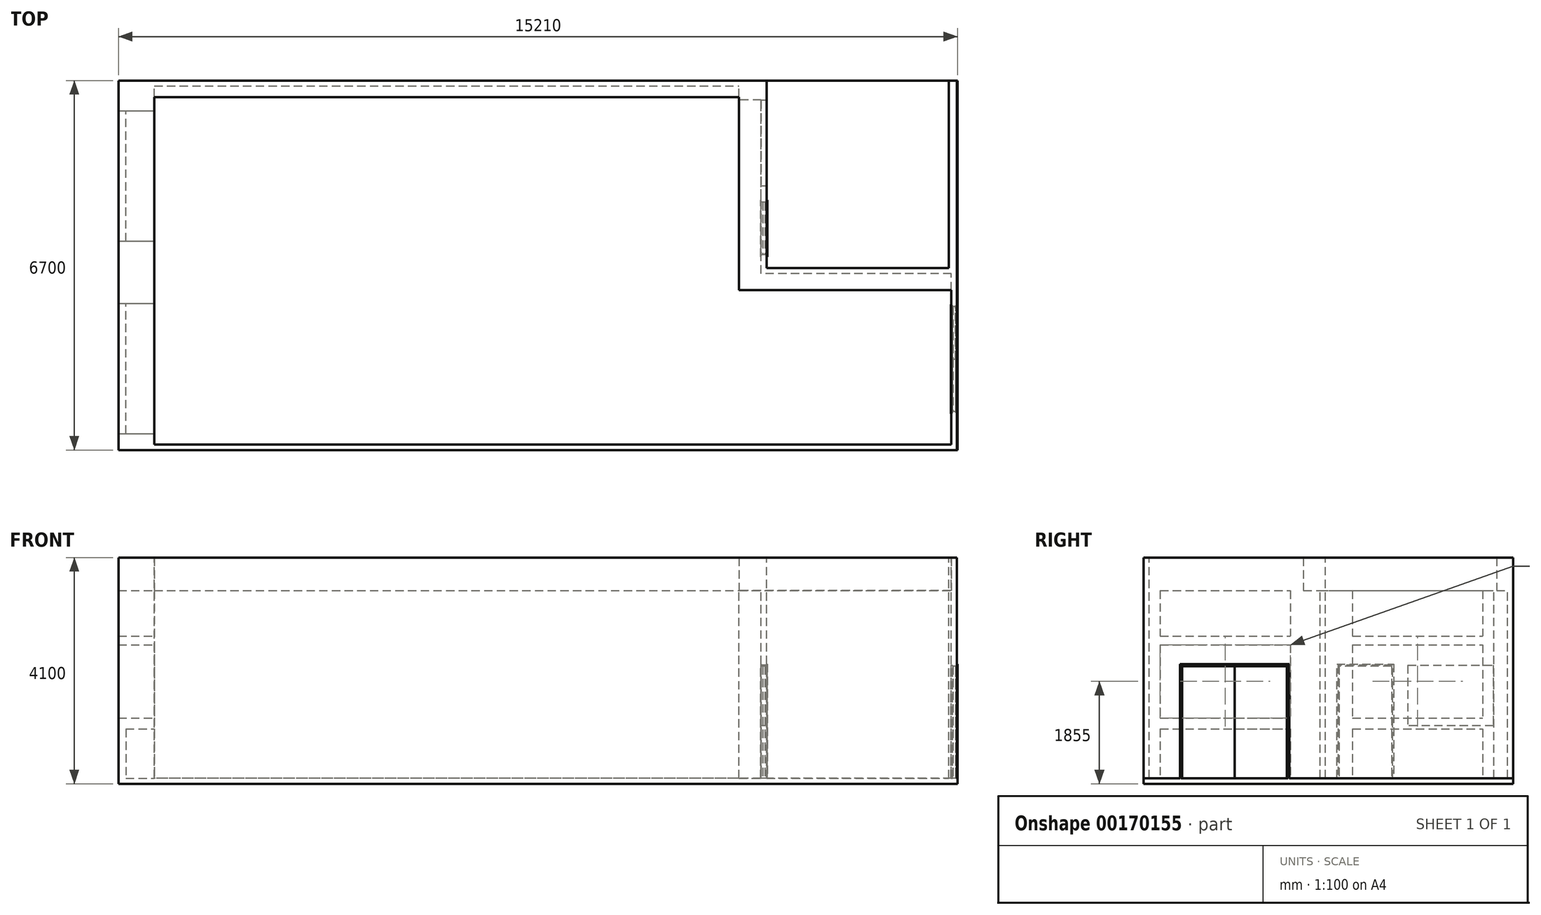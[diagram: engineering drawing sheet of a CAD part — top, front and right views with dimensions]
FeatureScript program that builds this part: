
annotation { "Feature Type Name" : "Feature", "Feature Type Description" : "" }
export const myFeature = defineFeature(function(context is Context, id is Id, definition is map)
    precondition{}
    {
        {
            var Q0;
            Q0=qCreatedBy(makeId("Right.planeOp"),FACE);
            var sketch = newSketch(context, id + "F0", { "sketchPlane" : qUnion([Q0])});
            skLineSegment(sketch, "E0", {"start": v(0, 0) * mm, "end": v(0, 4000) * mm});
            skLineSegment(sketch, "E1", {"start": v(6500, 4000) * mm, "end": v(6500, 0) * mm});
            skLineSegment(sketch, "E2", {"start": v(0, 0) * mm, "end": v(6500, 0) * mm});
            skLineSegment(sketch, "E3", {"start": v(0, 4000) * mm, "end": v(-100, 4000) * mm});
            skLineSegment(sketch, "E4", {"start": v(-100, 4000) * mm, "end": v(-100, -100) * mm});
            skLineSegment(sketch, "E5", {"start": v(-100, -100) * mm, "end": v(6600, -100) * mm});
            skLineSegment(sketch, "E6", {"start": v(6600, -100) * mm, "end": v(6600, 4000) * mm});
            skLineSegment(sketch, "E7", {"start": v(6600, 4000) * mm, "end": v(6500, 4000) * mm});
            skSolve(sketch);
        }
        {
            var Q0;
            Q0=makeQuery(id+"F0.imprint","IMPRINT",FACE,{"disambiguationData":[TD([[makeQuery(id+"F0.imprint","IMPRINT",EDGE,{"derivedFrom":sQuery(id+"F0.wireOp",EDGE,"E0")}),1.0]])]});
            extrude(context, id + "F1", {"entities" : qUnion([Q0]), "depth" : 14500 * mm});
        }
        {
            var Q0;
            Q0=makeQuery(id+"F1.opExtrude","CAP_FACE",FACE,{"disambiguationData":[OSD([sQuery(id+"F0.wireOp",EDGE,"E0"),sQuery(id+"F0.wireOp",EDGE,"E1"),sQuery(id+"F0.wireOp",EDGE,"E2"),sQuery(id+"F0.wireOp",EDGE,"E3"),sQuery(id+"F0.wireOp",EDGE,"E4"),sQuery(id+"F0.wireOp",EDGE,"E5"),sQuery(id+"F0.wireOp",EDGE,"E6"),sQuery(id+"F0.wireOp",EDGE,"E7")])],"isStart":true});
            var sketch = newSketch(context, id + "F2", { "sketchPlane" : qUnion([Q0])});
            skLineSegment(sketch, "E8.bottom", {"start": v(-6600, -100) * mm, "end": v(100, -100) * mm});
            skLineSegment(sketch, "E8.top", {"start": v(-6600, 4000) * mm, "end": v(100, 4000) * mm});
            skLineSegment(sketch, "E8.left", {"start": v(-6600, -100) * mm, "end": v(-6600, 4000) * mm});
            skLineSegment(sketch, "E8.right", {"start": v(100, -100) * mm, "end": v(100, 4000) * mm});
            skSolve(sketch);
        }
        {
            var Q0;
            Q0 = qSketchRegion(id + "F2", true);
            extrude(context, id + "F3", {"entities" : qUnion([Q0]), "operationType" : NewBodyOperationType.ADD, "depth" : 100 * mm});
        }
        {
            var Q0;
            Q0=makeQuery(id+"F1.opExtrude","CAP_FACE",FACE,{"disambiguationData":[OSD([sQuery(id+"F0.wireOp",EDGE,"E0"),sQuery(id+"F0.wireOp",EDGE,"E1"),sQuery(id+"F0.wireOp",EDGE,"E2"),sQuery(id+"F0.wireOp",EDGE,"E3"),sQuery(id+"F0.wireOp",EDGE,"E4"),sQuery(id+"F0.wireOp",EDGE,"E5"),sQuery(id+"F0.wireOp",EDGE,"E6"),sQuery(id+"F0.wireOp",EDGE,"E7")])],"isStart":false});
            var sketch = newSketch(context, id + "F4", { "sketchPlane" : qUnion([Q0])});
            skLineSegment(sketch, "E9.bottom", {"start": v(6600, -100) * mm, "end": v(3100, -100) * mm});
            skLineSegment(sketch, "E9.top", {"start": v(6600, 4000) * mm, "end": v(3100, 4000) * mm});
            skLineSegment(sketch, "E9.left", {"start": v(6600, -100) * mm, "end": v(6600, 4000) * mm});
            skLineSegment(sketch, "E9.right", {"start": v(3100, -100) * mm, "end": v(3100, 4000) * mm});
            skSolve(sketch);
        }
        {
            var Q0;
            Q0 = qSketchRegion(id + "F4", true);
            extrude(context, id + "F5", {"entities" : qUnion([Q0]), "operationType" : NewBodyOperationType.ADD, "oppositeDirection" : true, "depth" : 3500 * mm});
        }
        {
            var Q0;
            Q0=makeQuery(id+"F5.boolean.opBoolean","MERGE",FACE,{"derivedFrom":[makeQuery(id+"F3.boolean.opBoolean","MERGE",FACE,{"derivedFrom":[makeQuery(id+"F1.opExtrude","SWEPT_FACE",FACE,{"disambiguationData":[OSD([sQuery(id+"F0.wireOp",EDGE,"E3")])]}),makeQuery(id+"F1.opExtrude","SWEPT_FACE",FACE,{"disambiguationData":[OSD([sQuery(id+"F0.wireOp",EDGE,"E7")])]}),makeQuery(id+"F3.opExtrude","SWEPT_FACE",FACE,{"disambiguationData":[OSD([sQuery(id+"F2.wireOp",EDGE,"E8.top")])]})]}),makeQuery(id+"F5.opExtrude","SWEPT_FACE",FACE,{"disambiguationData":[OSD([sQuery(id+"F4.wireOp",EDGE,"E9.top")])]})]});
            var sketch = newSketch(context, id + "F6", { "sketchPlane" : qUnion([Q0])});
            skLineSegment(sketch, "E10.bottom", {"start": v(11100, 6500) * mm, "end": v(14400, 6500) * mm});
            skLineSegment(sketch, "E10.top", {"start": v(11100, 3200) * mm, "end": v(14400, 3200) * mm});
            skLineSegment(sketch, "E10.left", {"start": v(11100, 6500) * mm, "end": v(11100, 3200) * mm});
            skLineSegment(sketch, "E10.right", {"start": v(14400, 6500) * mm, "end": v(14400, 3200) * mm});
            skSolve(sketch);
        }
        {
            var Q0;
            Q0 = qSketchRegion(id + "F6", true);
            extrude(context, id + "F7", {"entities" : qUnion([Q0]), "operationType" : NewBodyOperationType.REMOVE, "oppositeDirection" : true, "depth" : 4000 * mm});
        }
        {
            var Q0;
            Q0=makeQuery(id+"F7.boolean.opBoolean","COPY",FACE,{"derivedFrom":makeQuery(id+"F7.opExtrude","SWEPT_FACE",FACE,{"disambiguationData":[OSD([sQuery(id+"F6.wireOp",EDGE,"E10.bottom")])]})});
            var sketch = newSketch(context, id + "F8", { "sketchPlane" : qUnion([Q0])});
            skLineSegment(sketch, "E11.bottom", {"start": v(11100, 4000) * mm, "end": v(14500, 4000) * mm});
            skLineSegment(sketch, "E11.top", {"start": v(11100, 0) * mm, "end": v(14500, 0) * mm});
            skLineSegment(sketch, "E11.left", {"start": v(11100, 4000) * mm, "end": v(11100, 0) * mm});
            skLineSegment(sketch, "E11.right", {"start": v(14500, 4000) * mm, "end": v(14500, 0) * mm});
            skLineSegment(sketch, "E12", {"start": v(14400, 4000) * mm, "end": v(14400, 0) * mm});
            skSolve(sketch);
        }
        {
            var Q0;
            {var subQ0=sQuery(id+"F8.wireOp",EDGE,"E11.left");Q0=makeQuery(id+"F8.imprint","IMPRINT",FACE,{"disambiguationData":[TD([[makeQuery(id+"F8.imprint","IMPRINT",EDGE,{"derivedFrom":subQ0}),-1.0]])]});}
            extrude(context, id + "F9", {"entities" : qUnion([Q0]), "operationType" : NewBodyOperationType.REMOVE, "oppositeDirection" : true, "depth" : 300 * mm});
        }
        {
            var Q0;
            Q0=makeQuery(id+"F5.boolean.opBoolean","MERGE",FACE,{"derivedFrom":[makeQuery(id+"F1.opExtrude","CAP_FACE",FACE,{"disambiguationData":[OSD([sQuery(id+"F0.wireOp",EDGE,"E0"),sQuery(id+"F0.wireOp",EDGE,"E1"),sQuery(id+"F0.wireOp",EDGE,"E2"),sQuery(id+"F0.wireOp",EDGE,"E3"),sQuery(id+"F0.wireOp",EDGE,"E4"),sQuery(id+"F0.wireOp",EDGE,"E5"),sQuery(id+"F0.wireOp",EDGE,"E6"),sQuery(id+"F0.wireOp",EDGE,"E7")])],"isStart":false}),makeQuery(id+"F5.opExtrude","CAP_FACE",FACE,{"disambiguationData":[OSD([sQuery(id+"F4.wireOp",EDGE,"E9.bottom"),sQuery(id+"F4.wireOp",EDGE,"E9.top"),sQuery(id+"F4.wireOp",EDGE,"E9.left"),sQuery(id+"F4.wireOp",EDGE,"E9.right")])],"isStart":true})]});
            var sketch = newSketch(context, id + "F10", { "sketchPlane" : qUnion([Q0])});
            skLineSegment(sketch, "E13.bottom", {"start": v(1550, 0) * mm, "end": v(2500, 0) * mm});
            skLineSegment(sketch, "E13.top", {"start": v(1550, 2020) * mm, "end": v(2500, 2020) * mm});
            skLineSegment(sketch, "E13.left", {"start": v(1550, 0) * mm, "end": v(1550, 2020) * mm});
            skLineSegment(sketch, "E13.right", {"start": v(2500, 0) * mm, "end": v(2500, 2020) * mm});
            skLineSegment(sketch, "E14", {"start": v(2500, 0) * mm, "end": v(2540, 0) * mm});
            skLineSegment(sketch, "E15", {"start": v(2540, 0) * mm, "end": v(2540, 2020) * mm});
            skLineSegment(sketch, "E16", {"start": v(2540, 2020) * mm, "end": v(2540, 2070) * mm});
            skLineSegment(sketch, "E17", {"start": v(2540, 2070) * mm, "end": v(1550, 2070) * mm});
            skLineSegment(sketch, "E18", {"start": v(1550, -782.26) * mm, "end": v(1550, 1451.07) * mm, "construction": true});
            skLineSegment(sketch, "E19.MirrorCS", {"start": v(600, 0) * mm, "end": v(600, 2020) * mm});
            skLineSegment(sketch, "E20.MirrorCS", {"start": v(560, 0) * mm, "end": v(560, 2020) * mm});
            skLineSegment(sketch, "E21.MirrorCS", {"start": v(600, 0) * mm, "end": v(560, 0) * mm});
            skLineSegment(sketch, "E22.MirrorCS", {"start": v(560, 2070) * mm, "end": v(1550, 2070) * mm});
            skLineSegment(sketch, "E23.MirrorCS", {"start": v(1550, 2020) * mm, "end": v(600, 2020) * mm});
            skLineSegment(sketch, "E24.MirrorCS", {"start": v(560, 2020) * mm, "end": v(560, 2070) * mm});
            skLineSegment(sketch, "E25", {"start": v(600, 2020) * mm, "end": v(596, 2020) * mm});
            skLineSegment(sketch, "E26", {"start": v(596, 2020) * mm, "end": v(596, 0) * mm});
            skLineSegment(sketch, "E27", {"start": v(2500, 2020) * mm, "end": v(2504, 2020) * mm});
            skLineSegment(sketch, "E28", {"start": v(2504, 2020) * mm, "end": v(2504, 0) * mm});
            skLineSegment(sketch, "E29", {"start": v(2520, 0) * mm, "end": v(2520, 2050) * mm});
            skPoint(sketch, "E29.endSnap0", {"position": v(2520, 0) * mm});
            skLineSegment(sketch, "E30", {"start": v(2520, 2050) * mm, "end": v(580, 2050) * mm});
            skLineSegment(sketch, "E31", {"start": v(580, 2050) * mm, "end": v(580, 0) * mm});
            skSolve(sketch);
        }
        {
            var Q0;
            {var subQ5=sQuery(id+"F10.wireOp",EDGE,"E15");Q0=makeQuery(id+"F10.imprint","IMPRINT",FACE,{"disambiguationData":[TD([[makeQuery(id+"F10.imprint","IMPRINT",EDGE,{"derivedFrom":subQ5}),1.0]])]});}
            extrude(context, id + "F11", {"entities" : qUnion([Q0]), "oppositeDirection" : true, "depth" : 60 * mm, "hasSecondDirection" : true, "secondDirectionOppositeDirection" : false, "secondDirectionDepth" : 60 * mm});
        }
        {
            var Q0;
            Q0=makeQuery(id+"F5.boolean.opBoolean","MERGE",FACE,{"derivedFrom":[makeQuery(id+"F1.opExtrude","CAP_FACE",FACE,{"disambiguationData":[OSD([sQuery(id+"F0.wireOp",EDGE,"E0"),sQuery(id+"F0.wireOp",EDGE,"E1"),sQuery(id+"F0.wireOp",EDGE,"E2"),sQuery(id+"F0.wireOp",EDGE,"E3"),sQuery(id+"F0.wireOp",EDGE,"E4"),sQuery(id+"F0.wireOp",EDGE,"E5"),sQuery(id+"F0.wireOp",EDGE,"E6"),sQuery(id+"F0.wireOp",EDGE,"E7")])],"isStart":false}),makeQuery(id+"F5.opExtrude","CAP_FACE",FACE,{"disambiguationData":[OSD([sQuery(id+"F4.wireOp",EDGE,"E9.bottom"),sQuery(id+"F4.wireOp",EDGE,"E9.top"),sQuery(id+"F4.wireOp",EDGE,"E9.left"),sQuery(id+"F4.wireOp",EDGE,"E9.right")])],"isStart":true})]});
            var sketch = newSketch(context, id + "F12", { "sketchPlane" : qUnion([Q0])});
            skLineSegment(sketch, "E32", {"start": v(2520, 0) * mm, "end": v(2520, 2050) * mm});
            skLineSegment(sketch, "E33", {"start": v(580, 0) * mm, "end": v(580, 2050) * mm});
            skLineSegment(sketch, "E34", {"start": v(580, 2050) * mm, "end": v(2520, 2050) * mm});
            skLineSegment(sketch, "E35", {"start": v(600, 2030) * mm, "end": v(2500, 2030) * mm});
            skLineSegment(sketch, "E36", {"start": v(2500, 2030) * mm, "end": v(2500, 0) * mm});
            skLineSegment(sketch, "E37", {"start": v(2500, 0) * mm, "end": v(2520, 0) * mm});
            skLineSegment(sketch, "E38", {"start": v(600, 2030) * mm, "end": v(600, 0) * mm});
            skLineSegment(sketch, "E39", {"start": v(600, 0) * mm, "end": v(580, 0) * mm});
            skSolve(sketch);
        }
        {
            var Q0;
            Q0=makeQuery(id+"F12.imprint","IMPRINT",FACE,{"disambiguationData":[TD([[makeQuery(id+"F12.imprint","IMPRINT",EDGE,{"derivedFrom":sQuery(id+"F12.wireOp",EDGE,"E32")}),1.0]])]});
            extrude(context, id + "F13", {"entities" : qUnion([Q0]), "operationType" : NewBodyOperationType.ADD, "depth" : 30 * mm, "hasSecondDirection" : true, "secondDirectionOppositeDirection" : true, "secondDirectionDepth" : 30 * mm});
        }
        {
            var Q0;
            Q0=makeQuery(id+"F5.boolean.opBoolean","MERGE",FACE,{"derivedFrom":[makeQuery(id+"F1.opExtrude","CAP_FACE",FACE,{"disambiguationData":[OSD([sQuery(id+"F0.wireOp",EDGE,"E0"),sQuery(id+"F0.wireOp",EDGE,"E1"),sQuery(id+"F0.wireOp",EDGE,"E2"),sQuery(id+"F0.wireOp",EDGE,"E3"),sQuery(id+"F0.wireOp",EDGE,"E4"),sQuery(id+"F0.wireOp",EDGE,"E5"),sQuery(id+"F0.wireOp",EDGE,"E6"),sQuery(id+"F0.wireOp",EDGE,"E7")])],"isStart":false}),makeQuery(id+"F5.opExtrude","CAP_FACE",FACE,{"disambiguationData":[OSD([sQuery(id+"F4.wireOp",EDGE,"E9.bottom"),sQuery(id+"F4.wireOp",EDGE,"E9.top"),sQuery(id+"F4.wireOp",EDGE,"E9.left"),sQuery(id+"F4.wireOp",EDGE,"E9.right")])],"isStart":true})]});
            var sketch = newSketch(context, id + "F14", { "sketchPlane" : qUnion([Q0])});
            skLineSegment(sketch, "E40", {"start": v(-100, 4000) * mm, "end": v(0, 4000) * mm});
            skLineSegment(sketch, "E41", {"start": v(0, 4000) * mm, "end": v(0, 0) * mm});
            skLineSegment(sketch, "E42", {"start": v(0, 0) * mm, "end": v(3100, 0) * mm});
            skLineSegment(sketch, "E43", {"start": v(3100, 0) * mm, "end": v(3100, 4000) * mm});
            skLineSegment(sketch, "E44", {"start": v(3100, 4000) * mm, "end": v(3300, 4000) * mm});
            skLineSegment(sketch, "E45", {"start": v(3300, 4000) * mm, "end": v(3300, 0) * mm});
            skLineSegment(sketch, "E46", {"start": v(3300, 0) * mm, "end": v(3300, -100) * mm});
            skLineSegment(sketch, "E47", {"start": v(3300, -100) * mm, "end": v(-100, -100) * mm});
            skLineSegment(sketch, "E48", {"start": v(-100, -100) * mm, "end": v(-100, 4000) * mm});
            skSolve(sketch);
        }
        {
            var Q0;
            Q0=makeQuery(id+"F14.imprint","IMPRINT",FACE,{"disambiguationData":[TD([[makeQuery(id+"F14.imprint","IMPRINT",EDGE,{"derivedFrom":sQuery(id+"F14.wireOp",EDGE,"E40")}),1.0]])]});
            var sketch = newSketch(context, id + "F15", { "sketchPlane" : qUnion([Q0])});
            skLineSegment(sketch, "E49", {"start": v(0, 0) * mm, "end": v(0, 4000) * mm});
            skLineSegment(sketch, "E50", {"start": v(0, 4000) * mm, "end": v(3100, 4000) * mm});
            skLineSegment(sketch, "E51", {"start": v(3100, 4000) * mm, "end": v(3100, 0) * mm});
            skLineSegment(sketch, "E52", {"start": v(3100, 0) * mm, "end": v(2540, 0) * mm});
            skLineSegment(sketch, "E53", {"start": v(2540, 0) * mm, "end": v(2540, 2070) * mm});
            skLineSegment(sketch, "E54", {"start": v(2540, 2070) * mm, "end": v(560, 2070) * mm});
            skLineSegment(sketch, "E55", {"start": v(560, 2070) * mm, "end": v(560, 0) * mm});
            skLineSegment(sketch, "E56", {"start": v(560, 0) * mm, "end": v(0, 0) * mm});
            skSolve(sketch);
        }
        {
            var Q0;
            Q0=makeQuery(id+"F15.imprint","IMPRINT",FACE,{"disambiguationData":[TD([[makeQuery(id+"F15.imprint","IMPRINT",EDGE,{"derivedFrom":sQuery(id+"F15.wireOp",EDGE,"E49")}),-1.0]])]});
            extrude(context, id + "F16", {"entities" : qUnion([Q0]), "operationType" : NewBodyOperationType.ADD, "oppositeDirection" : true, "depth" : 50 * mm});
        }
        {
            var Q0;
            Q0=makeQuery(id+"F16.boolean.opBoolean","MERGE",FACE,{"derivedFrom":[makeQuery(id+"F5.boolean.opBoolean","MERGE",FACE,{"derivedFrom":[makeQuery(id+"F1.opExtrude","CAP_FACE",FACE,{"disambiguationData":[OSD([sQuery(id+"F0.wireOp",EDGE,"E0"),sQuery(id+"F0.wireOp",EDGE,"E1"),sQuery(id+"F0.wireOp",EDGE,"E2"),sQuery(id+"F0.wireOp",EDGE,"E3"),sQuery(id+"F0.wireOp",EDGE,"E4"),sQuery(id+"F0.wireOp",EDGE,"E5"),sQuery(id+"F0.wireOp",EDGE,"E6"),sQuery(id+"F0.wireOp",EDGE,"E7")])],"isStart":false}),makeQuery(id+"F5.opExtrude","CAP_FACE",FACE,{"disambiguationData":[OSD([sQuery(id+"F4.wireOp",EDGE,"E9.bottom"),sQuery(id+"F4.wireOp",EDGE,"E9.top"),sQuery(id+"F4.wireOp",EDGE,"E9.left"),sQuery(id+"F4.wireOp",EDGE,"E9.right")])],"isStart":true})]}),makeQuery(id+"F16.opExtrude","CAP_FACE",FACE,{"disambiguationData":[OSD([sQuery(id+"F15.wireOp",EDGE,"E49"),sQuery(id+"F15.wireOp",EDGE,"E50"),sQuery(id+"F15.wireOp",EDGE,"E51"),sQuery(id+"F15.wireOp",EDGE,"E52"),sQuery(id+"F15.wireOp",EDGE,"E53"),sQuery(id+"F15.wireOp",EDGE,"E54"),sQuery(id+"F15.wireOp",EDGE,"E55"),sQuery(id+"F15.wireOp",EDGE,"E56")])],"isStart":true})]});
            var sketch = newSketch(context, id + "F17", { "sketchPlane" : qUnion([Q0])});
            skLineSegment(sketch, "E57.bottom", {"start": v(-100, 4000) * mm, "end": v(6600, 4000) * mm});
            skLineSegment(sketch, "E57.top", {"start": v(-100, -100) * mm, "end": v(6600, -100) * mm});
            skLineSegment(sketch, "E57.left", {"start": v(-100, 4000) * mm, "end": v(-100, -100) * mm});
            skLineSegment(sketch, "E57.right", {"start": v(6600, 4000) * mm, "end": v(6600, -100) * mm});
            skLineSegment(sketch, "E58.bottom", {"start": v(560, 2070) * mm, "end": v(2540, 2070) * mm});
            skLineSegment(sketch, "E58.top", {"start": v(560, 0) * mm, "end": v(2540, 0) * mm});
            skLineSegment(sketch, "E58.left", {"start": v(560, 2070) * mm, "end": v(560, 0) * mm});
            skLineSegment(sketch, "E58.right", {"start": v(2540, 2070) * mm, "end": v(2540, 0) * mm});
            skSolve(sketch);
        }
        {
            var Q0;
            Q0=makeQuery(id+"F17.imprint","IMPRINT",FACE,{"disambiguationData":[TD([[makeQuery(id+"F17.imprint","IMPRINT",EDGE,{"derivedFrom":sQuery(id+"F17.wireOp",EDGE,"E57.bottom")}),1.0]])]});
            extrude(context, id + "F18", {"entities" : qUnion([Q0]), "operationType" : NewBodyOperationType.ADD, "depth" : 50 * mm, "hasSecondDirection" : true, "secondDirectionOppositeDirection" : true, "secondDirectionDepth" : 50 * mm});
        }
        {
            var Q0;
            Q0=makeQuery(id+"F5.opExtrude","CAP_FACE",FACE,{"disambiguationData":[OSD([sQuery(id+"F4.wireOp",EDGE,"E9.bottom"),sQuery(id+"F4.wireOp",EDGE,"E9.top"),sQuery(id+"F4.wireOp",EDGE,"E9.left"),sQuery(id+"F4.wireOp",EDGE,"E9.right")])],"isStart":false});
            var sketch = newSketch(context, id + "F19", { "sketchPlane" : qUnion([Q0])});
            skLineSegment(sketch, "E59", {"start": v(-3405, 0) * mm, "end": v(-3405, 2070) * mm});
            skLineSegment(sketch, "E60", {"start": v(-3405, 2070) * mm, "end": v(-3445, 2070) * mm});
            skLineSegment(sketch, "E61", {"start": v(-3545, 0) * mm, "end": v(-3405, 0) * mm});
            skLineSegment(sketch, "E62", {"start": v(-4395, 2070) * mm, "end": v(-4435, 2070) * mm});
            skLineSegment(sketch, "E63", {"start": v(-4435, 2070) * mm, "end": v(-4435, 0) * mm});
            skLineSegment(sketch, "E64", {"start": v(-4495, 0) * mm, "end": v(-4435, 0) * mm});
            skLineSegment(sketch, "E65", {"start": v(-4395, 2070) * mm, "end": v(-3445, 2070) * mm});
            skLineSegment(sketch, "E66", {"start": v(-4495, 0) * mm, "end": v(-3545, 0) * mm});
            skSolve(sketch);
        }
        {
            var Q0;
            Q0 = qSketchRegion(id + "F19", true);
            var Q1;
            Q1=makeQuery(id+"F9.boolean.opBoolean","MERGE",FACE,{"derivedFrom":[makeQuery(id+"F7.boolean.opBoolean","COPY",FACE,{"derivedFrom":makeQuery(id+"F7.opExtrude","SWEPT_FACE",FACE,{"disambiguationData":[OSD([sQuery(id+"F6.wireOp",EDGE,"E10.left")])]})}),makeQuery(id+"F9.opExtrude","SWEPT_FACE",FACE,{"disambiguationData":[OSD([sQuery(id+"F8.wireOp",EDGE,"E11.left")])]})]});
            extrude(context, id + "F20", {"entities" : qUnion([Q0]), "operationType" : NewBodyOperationType.REMOVE, "endBound" : BoundingType.UP_TO_SURFACE, "oppositeDirection" : true, "endBoundEntityFace" : qUnion([Q1]), "depth" : 25 * mm});
        }
        {
            var Q0;
            Q0=makeQuery(id+"F20.boolean.opBoolean","MERGE",FACE,{"derivedFrom":[makeQuery(id+"F9.boolean.opBoolean","MERGE",FACE,{"derivedFrom":[makeQuery(id+"F7.boolean.opBoolean","COPY",FACE,{"derivedFrom":makeQuery(id+"F7.opExtrude","CAP_FACE",FACE,{"disambiguationData":[OSD([sQuery(id+"F6.wireOp",EDGE,"E10.bottom"),sQuery(id+"F6.wireOp",EDGE,"E10.top"),sQuery(id+"F6.wireOp",EDGE,"E10.left"),sQuery(id+"F6.wireOp",EDGE,"E10.right")])],"isStart":false})}),makeQuery(id+"F9.opExtrude","SWEPT_FACE",FACE,{"disambiguationData":[OSD([sQuery(id+"F8.wireOp",EDGE,"E11.top")])]})]}),makeQuery(id+"F18.boolean.opBoolean","MERGE",FACE,{"derivedFrom":[makeQuery(id+"F1.opExtrude","SWEPT_FACE",FACE,{"disambiguationData":[OSD([sQuery(id+"F0.wireOp",EDGE,"E2")])]}),makeQuery(id+"F18.opExtrude","SWEPT_FACE",FACE,{"disambiguationData":[OSD([sQuery(id+"F17.wireOp",EDGE,"E58.top")])]})]}),makeQuery(id+"F20.opExtrude","SWEPT_FACE",FACE,{"disambiguationData":[OSD([sQuery(id+"F19.wireOp",EDGE,"E61"),sQuery(id+"F19.wireOp",EDGE,"E64"),sQuery(id+"F19.wireOp",EDGE,"E66")])]})]});
            var sketch = newSketch(context, id + "F21", { "sketchPlane" : qUnion([Q0])});
            skLineSegment(sketch, "E67", {"start": v(14480, 2500) * mm, "end": v(14520, 2500) * mm});
            skLineSegment(sketch, "E68", {"start": v(14480, 2500) * mm, "end": v(14480, 1551) * mm});
            skLineSegment(sketch, "E69", {"start": v(14480, 1551) * mm, "end": v(14520, 1551) * mm});
            skLineSegment(sketch, "E70", {"start": v(14520, 1551) * mm, "end": v(14520, 2500) * mm});
            skLineSegment(sketch, "E71.bottom", {"start": v(14480, 1549) * mm, "end": v(14520, 1549) * mm});
            skLineSegment(sketch, "E71.top", {"start": v(14480, 600) * mm, "end": v(14520, 600) * mm});
            skLineSegment(sketch, "E71.left", {"start": v(14480, 1549) * mm, "end": v(14480, 600) * mm});
            skLineSegment(sketch, "E71.right", {"start": v(14520, 1549) * mm, "end": v(14520, 600) * mm});
            skSolve(sketch);
        }
        {
            var Q0;
            Q0 = qSketchRegion(id + "F21", true);
            var Q1;
            Q1=makeQuery(id+"F13.opExtrude","SWEPT_FACE",FACE,{"disambiguationData":[OSD([sQuery(id+"F12.wireOp",EDGE,"E35")])]});
            extrude(context, id + "F22", {"entities" : qUnion([Q0]), "endBound" : BoundingType.UP_TO_SURFACE, "endBoundEntityFace" : qUnion([Q1]), "depth" : 25 * mm});
        }
        {
            var Q0;
            Q0=makeQuery(id+"F18.opExtrude","CAP_FACE",FACE,{"disambiguationData":[OSD([sQuery(id+"F17.wireOp",EDGE,"E57.bottom"),sQuery(id+"F17.wireOp",EDGE,"E57.top"),sQuery(id+"F17.wireOp",EDGE,"E57.left"),sQuery(id+"F17.wireOp",EDGE,"E57.right"),sQuery(id+"F17.wireOp",EDGE,"E58.bottom"),sQuery(id+"F17.wireOp",EDGE,"E58.top"),sQuery(id+"F17.wireOp",EDGE,"E58.left"),sQuery(id+"F17.wireOp",EDGE,"E58.right")])],"isStart":false});
            var sketch = newSketch(context, id + "F23", { "sketchPlane" : qUnion([Q0])});
            skLineSegment(sketch, "E72.bottom", {"start": v(-100, -100) * mm, "end": v(6600, -100) * mm});
            skLineSegment(sketch, "E72.top", {"start": v(-100, 0) * mm, "end": v(6600, 0) * mm});
            skLineSegment(sketch, "E72.left", {"start": v(-100, -100) * mm, "end": v(-100, 0) * mm});
            skLineSegment(sketch, "E72.right", {"start": v(6600, -100) * mm, "end": v(6600, 0) * mm});
            skSolve(sketch);
        }
        {
            var Q0;
            Q0 = qSketchRegion(id + "F23", true);
            var Q1;
            Q1=makeQuery(id+"F11.opExtrude","CAP_FACE",FACE,{"disambiguationData":[OSD([sQuery(id+"F10.wireOp",EDGE,"E14"),sQuery(id+"F10.wireOp",EDGE,"E15"),sQuery(id+"F10.wireOp",EDGE,"E16"),sQuery(id+"F10.wireOp",EDGE,"E17"),sQuery(id+"F10.wireOp",EDGE,"E20.MirrorCS"),sQuery(id+"F10.wireOp",EDGE,"E21.MirrorCS"),sQuery(id+"F10.wireOp",EDGE,"E22.MirrorCS"),sQuery(id+"F10.wireOp",EDGE,"E24.MirrorCS"),sQuery(id+"F10.wireOp",EDGE,"E29"),sQuery(id+"F10.wireOp",EDGE,"E30"),sQuery(id+"F10.wireOp",EDGE,"E31")])],"isStart":true});
            extrude(context, id + "F24", {"entities" : qUnion([Q0]), "operationType" : NewBodyOperationType.ADD, "endBound" : BoundingType.UP_TO_SURFACE, "endBoundEntityFace" : qUnion([Q1]), "depth" : 25 * mm});
        }
        {
            var Q0;
            Q0=makeQuery(id+"F5.opExtrude","CAP_FACE",FACE,{"disambiguationData":[OSD([sQuery(id+"F4.wireOp",EDGE,"E9.bottom"),sQuery(id+"F4.wireOp",EDGE,"E9.top"),sQuery(id+"F4.wireOp",EDGE,"E9.left"),sQuery(id+"F4.wireOp",EDGE,"E9.right")])],"isStart":false});
            var sketch = newSketch(context, id + "F25", { "sketchPlane" : qUnion([Q0])});
            skLineSegment(sketch, "E73.bottom", {"start": v(-4435, 2070) * mm, "end": v(-3405, 2070) * mm});
            skLineSegment(sketch, "E73.left", {"start": v(-4435, 2070) * mm, "end": v(-4435, 0) * mm});
            skLineSegment(sketch, "E73.right", {"start": v(-3405, 2070) * mm, "end": v(-3405, 0) * mm});
            skLineSegment(sketch, "E74", {"start": v(-4435, 0) * mm, "end": v(-4415, 0) * mm});
            skLineSegment(sketch, "E75", {"start": v(-4415, 0) * mm, "end": v(-4415, 2050) * mm});
            skLineSegment(sketch, "E76", {"start": v(-4415, 2050) * mm, "end": v(-3425, 2050) * mm});
            skLineSegment(sketch, "E77", {"start": v(-3425, 2050) * mm, "end": v(-3425, 0) * mm});
            skLineSegment(sketch, "E78", {"start": v(-3425, 0) * mm, "end": v(-3405, 0) * mm});
            skSolve(sketch);
        }
        {
            var Q0;
            Q0 = qSketchRegion(id + "F25", true);
            extrude(context, id + "F26", {"entities" : qUnion([Q0]), "depth" : 10 * mm, "hasSecondDirection" : true, "secondDirectionOppositeDirection" : true, "secondDirectionDepth" : 110 * mm});
        }
        {
            var Q0;
            Q0=makeQuery(id+"F5.opExtrude","CAP_FACE",FACE,{"disambiguationData":[OSD([sQuery(id+"F4.wireOp",EDGE,"E9.bottom"),sQuery(id+"F4.wireOp",EDGE,"E9.top"),sQuery(id+"F4.wireOp",EDGE,"E9.left"),sQuery(id+"F4.wireOp",EDGE,"E9.right")])],"isStart":false});
            var sketch = newSketch(context, id + "F27", { "sketchPlane" : qUnion([Q0])});
            skLineSegment(sketch, "E79", {"start": v(-4415, 0) * mm, "end": v(-4415, 2050) * mm});
            skLineSegment(sketch, "E80", {"start": v(-4415, 2050) * mm, "end": v(-3425, 2050) * mm});
            skLineSegment(sketch, "E81", {"start": v(-3425, 2050) * mm, "end": v(-3425, 0) * mm});
            skLineSegment(sketch, "E82", {"start": v(-3425, 0) * mm, "end": v(-3445, 0) * mm});
            skLineSegment(sketch, "E83", {"start": v(-3445, 0) * mm, "end": v(-3445, 2030) * mm});
            skLineSegment(sketch, "E84", {"start": v(-3445, 2030) * mm, "end": v(-4395, 2030) * mm});
            skLineSegment(sketch, "E85", {"start": v(-4395, 2030) * mm, "end": v(-4395, 0) * mm});
            skLineSegment(sketch, "E86", {"start": v(-4395, 0) * mm, "end": v(-4415, 0) * mm});
            skSolve(sketch);
        }
        {
            var Q0;
            Q0 = qSketchRegion(id + "F27", true);
            extrude(context, id + "F28", {"entities" : qUnion([Q0]), "operationType" : NewBodyOperationType.ADD, "oppositeDirection" : true, "depth" : 100 * mm});
        }
        {
            var Q0;
            Q0=makeQuery(id+"F24.boolean.opBoolean","MERGE",FACE,{"derivedFrom":[makeQuery(id+"F20.boolean.opBoolean","MERGE",FACE,{"derivedFrom":[makeQuery(id+"F9.boolean.opBoolean","MERGE",FACE,{"derivedFrom":[makeQuery(id+"F7.boolean.opBoolean","COPY",FACE,{"derivedFrom":makeQuery(id+"F7.opExtrude","CAP_FACE",FACE,{"disambiguationData":[OSD([sQuery(id+"F6.wireOp",EDGE,"E10.bottom"),sQuery(id+"F6.wireOp",EDGE,"E10.top"),sQuery(id+"F6.wireOp",EDGE,"E10.left"),sQuery(id+"F6.wireOp",EDGE,"E10.right")])],"isStart":false})}),makeQuery(id+"F9.opExtrude","SWEPT_FACE",FACE,{"disambiguationData":[OSD([sQuery(id+"F8.wireOp",EDGE,"E11.top")])]})]}),makeQuery(id+"F18.boolean.opBoolean","MERGE",FACE,{"derivedFrom":[makeQuery(id+"F1.opExtrude","SWEPT_FACE",FACE,{"disambiguationData":[OSD([sQuery(id+"F0.wireOp",EDGE,"E2")])]}),makeQuery(id+"F18.opExtrude","SWEPT_FACE",FACE,{"disambiguationData":[OSD([sQuery(id+"F17.wireOp",EDGE,"E58.top")])]})]}),makeQuery(id+"F20.opExtrude","SWEPT_FACE",FACE,{"disambiguationData":[OSD([sQuery(id+"F19.wireOp",EDGE,"E61"),sQuery(id+"F19.wireOp",EDGE,"E66")])]})]}),makeQuery(id+"F24.opExtrude","SWEPT_FACE",FACE,{"disambiguationData":[OSD([sQuery(id+"F23.wireOp",EDGE,"E72.top")])]})]});
            var sketch = newSketch(context, id + "F29", { "sketchPlane" : qUnion([Q0])});
            skLineSegment(sketch, "E87.bottom", {"start": v(11030, 4395) * mm, "end": v(11070, 4395) * mm});
            skLineSegment(sketch, "E87.top", {"start": v(11030, 3445) * mm, "end": v(11070, 3445) * mm});
            skLineSegment(sketch, "E87.left", {"start": v(11030, 4395) * mm, "end": v(11030, 3445) * mm});
            skLineSegment(sketch, "E87.right", {"start": v(11070, 4395) * mm, "end": v(11070, 3445) * mm});
            skSolve(sketch);
        }
        {
            var Q0;
            Q0 = qSketchRegion(id + "F29", true);
            var Q1;
            Q1=makeQuery(id+"F28.opExtrude","SWEPT_FACE",FACE,{"disambiguationData":[OSD([sQuery(id+"F27.wireOp",EDGE,"E84")])]});
            extrude(context, id + "F30", {"entities" : qUnion([Q0]), "endBound" : BoundingType.UP_TO_SURFACE, "endBoundEntityFace" : qUnion([Q1]), "depth" : 25 * mm});
        }
        {
            var Q0;
            Q0=makeQuery(id+"F3.opExtrude","CAP_FACE",FACE,{"disambiguationData":[OSD([sQuery(id+"F2.wireOp",EDGE,"E8.bottom"),sQuery(id+"F2.wireOp",EDGE,"E8.top"),sQuery(id+"F2.wireOp",EDGE,"E8.left"),sQuery(id+"F2.wireOp",EDGE,"E8.right")])],"isStart":true});
            var sketch = newSketch(context, id + "F31", { "sketchPlane" : qUnion([Q0])});
            skLineSegment(sketch, "E88.bottom", {"start": v(200, 2420) * mm, "end": v(2562.5, 2420) * mm});
            skLineSegment(sketch, "E88.top", {"start": v(200, 1090) * mm, "end": v(2562.5, 1090) * mm});
            skLineSegment(sketch, "E88.left", {"start": v(200, 2420) * mm, "end": v(200, 1090) * mm});
            skLineSegment(sketch, "E88.right", {"start": v(2562.5, 2420) * mm, "end": v(2562.5, 1090) * mm});
            skLineSegment(sketch, "E89.bottom", {"start": v(3687.5, 2420) * mm, "end": v(6050, 2420) * mm});
            skLineSegment(sketch, "E89.top", {"start": v(3687.5, 1090) * mm, "end": v(6050, 1090) * mm});
            skLineSegment(sketch, "E89.left", {"start": v(3687.5, 2420) * mm, "end": v(3687.5, 1090) * mm});
            skLineSegment(sketch, "E89.right", {"start": v(6050, 2420) * mm, "end": v(6050, 1090) * mm});
            skSolve(sketch);
        }
        {
            var Q0;
            Q0 = qSketchRegion(id + "F31", true);
            var Q1;
            Q1=makeQuery(id+"F3.opExtrude","CAP_FACE",FACE,{"disambiguationData":[OSD([sQuery(id+"F2.wireOp",EDGE,"E8.bottom"),sQuery(id+"F2.wireOp",EDGE,"E8.top"),sQuery(id+"F2.wireOp",EDGE,"E8.left"),sQuery(id+"F2.wireOp",EDGE,"E8.right")])],"isStart":false});
            extrude(context, id + "F32", {"entities" : qUnion([Q0]), "operationType" : NewBodyOperationType.REMOVE, "endBound" : BoundingType.UP_TO_SURFACE, "oppositeDirection" : true, "endBoundEntityFace" : qUnion([Q1]), "depth" : 25 * mm});
        }
        {
            var Q0;
            Q0=makeQuery(id+"F3.opExtrude","CAP_FACE",FACE,{"disambiguationData":[OSD([sQuery(id+"F2.wireOp",EDGE,"E8.bottom"),sQuery(id+"F2.wireOp",EDGE,"E8.top"),sQuery(id+"F2.wireOp",EDGE,"E8.left"),sQuery(id+"F2.wireOp",EDGE,"E8.right")])],"isStart":true});
            var sketch = newSketch(context, id + "F33", { "sketchPlane" : qUnion([Q0])});
            skLineSegment(sketch, "E90.bottom", {"start": v(200, 3400) * mm, "end": v(2562.5, 3400) * mm});
            skLineSegment(sketch, "E90.top", {"start": v(200, 2575) * mm, "end": v(2562.5, 2575) * mm});
            skLineSegment(sketch, "E90.left", {"start": v(200, 3400) * mm, "end": v(200, 2575) * mm});
            skLineSegment(sketch, "E90.right", {"start": v(2562.5, 3400) * mm, "end": v(2562.5, 2575) * mm});
            skLineSegment(sketch, "E91.bottom", {"start": v(3687.5, 3400) * mm, "end": v(6050, 3400) * mm});
            skLineSegment(sketch, "E91.top", {"start": v(3687.5, 2575) * mm, "end": v(6050, 2575) * mm});
            skLineSegment(sketch, "E91.left", {"start": v(3687.5, 3400) * mm, "end": v(3687.5, 2575) * mm});
            skLineSegment(sketch, "E91.right", {"start": v(6050, 3400) * mm, "end": v(6050, 2575) * mm});
            skSolve(sketch);
        }
        {
            var Q0;
            Q0 = qSketchRegion(id + "F33", true);
            var Q1;
            Q1=makeQuery(id+"F3.opExtrude","CAP_FACE",FACE,{"disambiguationData":[OSD([sQuery(id+"F2.wireOp",EDGE,"E8.bottom"),sQuery(id+"F2.wireOp",EDGE,"E8.top"),sQuery(id+"F2.wireOp",EDGE,"E8.left"),sQuery(id+"F2.wireOp",EDGE,"E8.right")])],"isStart":false});
            extrude(context, id + "F34", {"entities" : qUnion([Q0]), "operationType" : NewBodyOperationType.REMOVE, "endBound" : BoundingType.UP_TO_SURFACE, "oppositeDirection" : true, "endBoundEntityFace" : qUnion([Q1]), "depth" : 25 * mm});
        }
        {
            var Q0;
            Q0=makeQuery(id+"F3.opExtrude","CAP_FACE",FACE,{"disambiguationData":[OSD([sQuery(id+"F2.wireOp",EDGE,"E8.bottom"),sQuery(id+"F2.wireOp",EDGE,"E8.top"),sQuery(id+"F2.wireOp",EDGE,"E8.left"),sQuery(id+"F2.wireOp",EDGE,"E8.right")])],"isStart":false});
            var sketch = newSketch(context, id + "F35", { "sketchPlane" : qUnion([Q0])});
            skLineSegment(sketch, "E92.bottom", {"start": v(-6600, 4000) * mm, "end": v(100, 4000) * mm});
            skLineSegment(sketch, "E92.top", {"start": v(-6600, -100) * mm, "end": v(100, -100) * mm});
            skLineSegment(sketch, "E92.left", {"start": v(-6600, 4000) * mm, "end": v(-6600, -100) * mm});
            skLineSegment(sketch, "E92.right", {"start": v(100, 4000) * mm, "end": v(100, -100) * mm});
            skLineSegment(sketch, "E93.bottom", {"start": v(-6050, 3400) * mm, "end": v(-3687.5, 3400) * mm});
            skLineSegment(sketch, "E93.top", {"start": v(-6050, 2575) * mm, "end": v(-3687.5, 2575) * mm});
            skLineSegment(sketch, "E93.left", {"start": v(-6050, 3400) * mm, "end": v(-6050, 2575) * mm});
            skLineSegment(sketch, "E93.right", {"start": v(-3687.5, 3400) * mm, "end": v(-3687.5, 2575) * mm});
            skLineSegment(sketch, "E94.bottom", {"start": v(-2562.5, 3400) * mm, "end": v(-200, 3400) * mm});
            skLineSegment(sketch, "E94.top", {"start": v(-2562.5, 2575) * mm, "end": v(-200, 2575) * mm});
            skLineSegment(sketch, "E94.left", {"start": v(-2562.5, 3400) * mm, "end": v(-2562.5, 2575) * mm});
            skLineSegment(sketch, "E94.right", {"start": v(-200, 3400) * mm, "end": v(-200, 2575) * mm});
            skLineSegment(sketch, "E95.bottom", {"start": v(-200, 2420) * mm, "end": v(-2562.5, 2420) * mm});
            skLineSegment(sketch, "E95.top", {"start": v(-200, 1090) * mm, "end": v(-2562.5, 1090) * mm});
            skLineSegment(sketch, "E95.left", {"start": v(-200, 2420) * mm, "end": v(-200, 1090) * mm});
            skLineSegment(sketch, "E95.right", {"start": v(-2562.5, 2420) * mm, "end": v(-2562.5, 1090) * mm});
            skLineSegment(sketch, "E96.bottom", {"start": v(-3687.5, 2420) * mm, "end": v(-6050, 2420) * mm});
            skLineSegment(sketch, "E96.top", {"start": v(-3687.5, 1090) * mm, "end": v(-6050, 1090) * mm});
            skLineSegment(sketch, "E96.left", {"start": v(-3687.5, 2420) * mm, "end": v(-3687.5, 1090) * mm});
            skLineSegment(sketch, "E96.right", {"start": v(-6050, 2420) * mm, "end": v(-6050, 1090) * mm});
            skSolve(sketch);
        }
        {
            var Q0;
            Q0 = qSketchRegion(id + "F35", true);
            extrude(context, id + "F36", {"entities" : qUnion([Q0]), "operationType" : NewBodyOperationType.ADD, "depth" : 35 * mm});
        }
        {
            var Q0;
            Q0=makeQuery(id+"F36.opExtrude","CAP_FACE",FACE,{"disambiguationData":[OSD([sQuery(id+"F35.wireOp",EDGE,"E92.bottom"),sQuery(id+"F35.wireOp",EDGE,"E92.top"),sQuery(id+"F35.wireOp",EDGE,"E92.left"),sQuery(id+"F35.wireOp",EDGE,"E92.right"),sQuery(id+"F35.wireOp",EDGE,"E93.bottom"),sQuery(id+"F35.wireOp",EDGE,"E93.top"),sQuery(id+"F35.wireOp",EDGE,"E93.left"),sQuery(id+"F35.wireOp",EDGE,"E93.right"),sQuery(id+"F35.wireOp",EDGE,"E94.bottom"),sQuery(id+"F35.wireOp",EDGE,"E94.top"),sQuery(id+"F35.wireOp",EDGE,"E94.left"),sQuery(id+"F35.wireOp",EDGE,"E94.right"),sQuery(id+"F35.wireOp",EDGE,"E95.bottom"),sQuery(id+"F35.wireOp",EDGE,"E95.top"),sQuery(id+"F35.wireOp",EDGE,"E95.left"),sQuery(id+"F35.wireOp",EDGE,"E95.right"),sQuery(id+"F35.wireOp",EDGE,"E96.bottom"),sQuery(id+"F35.wireOp",EDGE,"E96.top"),sQuery(id+"F35.wireOp",EDGE,"E96.left"),sQuery(id+"F35.wireOp",EDGE,"E96.right")])],"isStart":false});
            var sketch = newSketch(context, id + "F37", { "sketchPlane" : qUnion([Q0])});
            skLineSegment(sketch, "E97.bottom", {"start": v(-6600, -100) * mm, "end": v(100, -100) * mm});
            skLineSegment(sketch, "E97.left", {"start": v(-6600, -100) * mm, "end": v(-6600, 4000) * mm});
            skLineSegment(sketch, "E98", {"start": v(-6600, 4000) * mm, "end": v(100, 4000) * mm});
            skLineSegment(sketch, "E99.bottom", {"start": v(-6050, 3400) * mm, "end": v(-3687.5, 3400) * mm});
            skLineSegment(sketch, "E99.top", {"start": v(-6050, 2575) * mm, "end": v(-3687.5, 2575) * mm});
            skLineSegment(sketch, "E99.left", {"start": v(-6050, 3400) * mm, "end": v(-6050, 2575) * mm});
            skLineSegment(sketch, "E99.right", {"start": v(-3687.5, 3400) * mm, "end": v(-3687.5, 2575) * mm});
            skLineSegment(sketch, "E100.bottom", {"start": v(-2562.5, 3400) * mm, "end": v(-200, 3400) * mm});
            skLineSegment(sketch, "E100.top", {"start": v(-2562.5, 2575) * mm, "end": v(-200, 2575) * mm});
            skLineSegment(sketch, "E100.left", {"start": v(-2562.5, 3400) * mm, "end": v(-2562.5, 2575) * mm});
            skLineSegment(sketch, "E100.right", {"start": v(-200, 3400) * mm, "end": v(-200, 2575) * mm});
            skLineSegment(sketch, "E101.bottom", {"start": v(-2562.5, 2420) * mm, "end": v(-200, 2420) * mm});
            skLineSegment(sketch, "E101.top", {"start": v(-2562.5, 1090) * mm, "end": v(-200, 1090) * mm});
            skLineSegment(sketch, "E101.left", {"start": v(-2562.5, 2420) * mm, "end": v(-2562.5, 1090) * mm});
            skLineSegment(sketch, "E101.right", {"start": v(-200, 2420) * mm, "end": v(-200, 1090) * mm});
            skLineSegment(sketch, "E102.bottom", {"start": v(-6050, 2420) * mm, "end": v(-3687.5, 2420) * mm});
            skLineSegment(sketch, "E102.top", {"start": v(-6050, 1090) * mm, "end": v(-3687.5, 1090) * mm});
            skLineSegment(sketch, "E102.left", {"start": v(-6050, 2420) * mm, "end": v(-6050, 1090) * mm});
            skLineSegment(sketch, "E102.right", {"start": v(-3687.5, 2420) * mm, "end": v(-3687.5, 1090) * mm});
            skLineSegment(sketch, "E103", {"start": v(100, 4000) * mm, "end": v(100, -100) * mm});
            skSolve(sketch);
        }
        {
            var Q0;
            Q0 = qSketchRegion(id + "F37", true);
            extrude(context, id + "F38", {"entities" : qUnion([Q0]), "operationType" : NewBodyOperationType.ADD, "depth" : 515 * mm});
        }
        {
            var Q0;
            Q0=makeQuery(id+"F3.opExtrude","CAP_FACE",FACE,{"disambiguationData":[OSD([sQuery(id+"F2.wireOp",EDGE,"E8.bottom"),sQuery(id+"F2.wireOp",EDGE,"E8.top"),sQuery(id+"F2.wireOp",EDGE,"E8.left"),sQuery(id+"F2.wireOp",EDGE,"E8.right")])],"isStart":true});
            var sketch = newSketch(context, id + "F39", { "sketchPlane" : qUnion([Q0])});
            skLineSegment(sketch, "E104.bottom", {"start": v(200, 895) * mm, "end": v(2562.5, 895) * mm});
            skLineSegment(sketch, "E104.top", {"start": v(200, 0) * mm, "end": v(2562.5, 0) * mm});
            skLineSegment(sketch, "E104.left", {"start": v(200, 895) * mm, "end": v(200, 0) * mm});
            skLineSegment(sketch, "E104.right", {"start": v(2562.5, 895) * mm, "end": v(2562.5, 0) * mm});
            skLineSegment(sketch, "E105.bottom", {"start": v(3687.5, 895) * mm, "end": v(6050, 895) * mm});
            skLineSegment(sketch, "E105.top", {"start": v(3687.5, 0) * mm, "end": v(6050, 0) * mm});
            skLineSegment(sketch, "E105.left", {"start": v(3687.5, 895) * mm, "end": v(3687.5, 0) * mm});
            skLineSegment(sketch, "E105.right", {"start": v(6050, 895) * mm, "end": v(6050, 0) * mm});
            skSolve(sketch);
        }
        {
            var Q0;
            Q0 = qSketchRegion(id + "F39", true);
            extrude(context, id + "F40", {"entities" : qUnion([Q0]), "operationType" : NewBodyOperationType.REMOVE, "oppositeDirection" : true, "depth" : 515 * mm});
        }
        {
            var Q0;
            Q0=makeQuery(id+"F1.opExtrude","SWEPT_FACE",FACE,{"disambiguationData":[OSD([sQuery(id+"F0.wireOp",EDGE,"E1")])]});
            var sketch = newSketch(context, id + "F41", { "sketchPlane" : qUnion([Q0])});
            skLineSegment(sketch, "E106.bottom", {"start": v(10600, 4000) * mm, "end": v(11000, 4000) * mm});
            skLineSegment(sketch, "E106.top", {"start": v(10600, 3400) * mm, "end": v(11000, 3400) * mm});
            skLineSegment(sketch, "E106.left", {"start": v(10600, 4000) * mm, "end": v(10600, 3400) * mm});
            skLineSegment(sketch, "E106.right", {"start": v(11000, 4000) * mm, "end": v(11000, 3400) * mm});
            skSolve(sketch);
        }
        {
            var Q0;
            Q0 = qSketchRegion(id + "F41", true);
            var Q1;
            Q1=makeQuery(id+"F1.opExtrude","SWEPT_FACE",FACE,{"disambiguationData":[OSD([sQuery(id+"F0.wireOp",EDGE,"E0")])]});
            extrude(context, id + "F42", {"entities" : qUnion([Q0]), "operationType" : NewBodyOperationType.ADD, "endBoundEntityFace" : qUnion([Q1]), "depth" : 3700 * mm});
        }
        {
            var Q0;
            Q0=makeQuery(id+"F42.opExtrude","SWEPT_FACE",FACE,{"disambiguationData":[OSD([sQuery(id+"F41.wireOp",EDGE,"E106.right")])]});
            var sketch = newSketch(context, id + "F43", { "sketchPlane" : qUnion([Q0])});
            skLineSegment(sketch, "E107.bottom", {"start": v(2800, 4000) * mm, "end": v(3100, 4000) * mm});
            skLineSegment(sketch, "E107.top", {"start": v(2800, 3400) * mm, "end": v(3100, 3400) * mm});
            skLineSegment(sketch, "E107.left", {"start": v(2800, 4000) * mm, "end": v(2800, 3400) * mm});
            skLineSegment(sketch, "E107.right", {"start": v(3100, 4000) * mm, "end": v(3100, 3400) * mm});
            skSolve(sketch);
        }
        {
            var Q0;
            Q0 = qSketchRegion(id + "F43", true);
            var Q1;
            Q1=makeQuery(id+"F16.opExtrude","CAP_FACE",FACE,{"disambiguationData":[OSD([sQuery(id+"F15.wireOp",EDGE,"E49"),sQuery(id+"F15.wireOp",EDGE,"E50"),sQuery(id+"F15.wireOp",EDGE,"E51"),sQuery(id+"F15.wireOp",EDGE,"E52"),sQuery(id+"F15.wireOp",EDGE,"E53"),sQuery(id+"F15.wireOp",EDGE,"E54"),sQuery(id+"F15.wireOp",EDGE,"E55"),sQuery(id+"F15.wireOp",EDGE,"E56")])],"isStart":false});
            extrude(context, id + "F44", {"entities" : qUnion([Q0]), "operationType" : NewBodyOperationType.ADD, "endBound" : BoundingType.UP_TO_SURFACE, "endBoundEntityFace" : qUnion([Q1]), "depth" : 25 * mm});
        }
        {
            var Q0;
            Q0=makeQuery(id+"F42.opExtrude","SWEPT_FACE",FACE,{"disambiguationData":[OSD([sQuery(id+"F41.wireOp",EDGE,"E106.left")])]});
            var sketch = newSketch(context, id + "F45", { "sketchPlane" : qUnion([Q0])});
            skLineSegment(sketch, "E108.bottom", {"start": v(-6500, 4000) * mm, "end": v(-6300, 4000) * mm});
            skLineSegment(sketch, "E108.top", {"start": v(-6500, 3400) * mm, "end": v(-6300, 3400) * mm});
            skLineSegment(sketch, "E108.left", {"start": v(-6500, 4000) * mm, "end": v(-6500, 3400) * mm});
            skLineSegment(sketch, "E108.right", {"start": v(-6300, 4000) * mm, "end": v(-6300, 3400) * mm});
            skSolve(sketch);
        }
        {
            var Q0;
            Q0 = qSketchRegion(id + "F45", true);
            var Q1;
            Q1=makeQuery(id+"F3.opExtrude","CAP_FACE",FACE,{"disambiguationData":[OSD([sQuery(id+"F2.wireOp",EDGE,"E8.bottom"),sQuery(id+"F2.wireOp",EDGE,"E8.top"),sQuery(id+"F2.wireOp",EDGE,"E8.left"),sQuery(id+"F2.wireOp",EDGE,"E8.right")])],"isStart":true});
            extrude(context, id + "F46", {"entities" : qUnion([Q0]), "operationType" : NewBodyOperationType.ADD, "endBound" : BoundingType.UP_TO_SURFACE, "endBoundEntityFace" : qUnion([Q1]), "depth" : 25 * mm});
        }
        {
            var Q0;
            Q0=makeQuery(id+"F46.boolean.opBoolean","MERGE",FACE,{"derivedFrom":[makeQuery(id+"F44.boolean.opBoolean","MERGE",FACE,{"derivedFrom":[makeQuery(id+"F42.opExtrude","SWEPT_FACE",FACE,{"disambiguationData":[OSD([sQuery(id+"F41.wireOp",EDGE,"E106.top")])]}),makeQuery(id+"F44.opExtrude","SWEPT_FACE",FACE,{"disambiguationData":[OSD([sQuery(id+"F43.wireOp",EDGE,"E107.top")])]})]}),makeQuery(id+"F46.opExtrude","SWEPT_FACE",FACE,{"disambiguationData":[OSD([sQuery(id+"F45.wireOp",EDGE,"E108.top")])]})]});
            var sketch = newSketch(context, id + "F47", { "sketchPlane" : qUnion([Q0])});
            skLineSegment(sketch, "E109.bottom", {"start": v(11000, -6500) * mm, "end": v(10600, -6500) * mm});
            skLineSegment(sketch, "E109.top", {"start": v(11000, -6250) * mm, "end": v(10600, -6250) * mm});
            skLineSegment(sketch, "E109.left", {"start": v(11000, -6500) * mm, "end": v(11000, -6250) * mm});
            skLineSegment(sketch, "E109.right", {"start": v(10600, -6500) * mm, "end": v(10600, -6250) * mm});
            skSolve(sketch);
        }
        {
            var Q0;
            Q0 = qSketchRegion(id + "F47", true);
            var Q1;
            Q1=makeQuery(id+"F40.boolean.opBoolean","MERGE",FACE,{"derivedFrom":[makeQuery(id+"F24.boolean.opBoolean","MERGE",FACE,{"derivedFrom":[makeQuery(id+"F20.boolean.opBoolean","MERGE",FACE,{"derivedFrom":[makeQuery(id+"F9.boolean.opBoolean","MERGE",FACE,{"derivedFrom":[makeQuery(id+"F7.boolean.opBoolean","COPY",FACE,{"derivedFrom":makeQuery(id+"F7.opExtrude","CAP_FACE",FACE,{"disambiguationData":[OSD([sQuery(id+"F6.wireOp",EDGE,"E10.bottom"),sQuery(id+"F6.wireOp",EDGE,"E10.top"),sQuery(id+"F6.wireOp",EDGE,"E10.left"),sQuery(id+"F6.wireOp",EDGE,"E10.right")])],"isStart":false})}),makeQuery(id+"F9.opExtrude","SWEPT_FACE",FACE,{"disambiguationData":[OSD([sQuery(id+"F8.wireOp",EDGE,"E11.top")])]})]}),makeQuery(id+"F18.boolean.opBoolean","MERGE",FACE,{"derivedFrom":[makeQuery(id+"F1.opExtrude","SWEPT_FACE",FACE,{"disambiguationData":[OSD([sQuery(id+"F0.wireOp",EDGE,"E2")])]}),makeQuery(id+"F18.opExtrude","SWEPT_FACE",FACE,{"disambiguationData":[OSD([sQuery(id+"F17.wireOp",EDGE,"E58.top")])]})]}),makeQuery(id+"F20.opExtrude","SWEPT_FACE",FACE,{"disambiguationData":[OSD([sQuery(id+"F19.wireOp",EDGE,"E61"),sQuery(id+"F19.wireOp",EDGE,"E66")])]})]}),makeQuery(id+"F24.opExtrude","SWEPT_FACE",FACE,{"disambiguationData":[OSD([sQuery(id+"F23.wireOp",EDGE,"E72.top")])]})]}),makeQuery(id+"F40.opExtrude","SWEPT_FACE",FACE,{"disambiguationData":[OSD([sQuery(id+"F39.wireOp",EDGE,"E104.top")])]}),makeQuery(id+"F40.opExtrude","SWEPT_FACE",FACE,{"disambiguationData":[OSD([sQuery(id+"F39.wireOp",EDGE,"E105.top")])]})]});
            extrude(context, id + "F48", {"entities" : qUnion([Q0]), "operationType" : NewBodyOperationType.ADD, "endBound" : BoundingType.UP_TO_SURFACE, "endBoundEntityFace" : qUnion([Q1]), "depth" : 25 * mm});
        }
        {
            var Q0;
            Q0=makeQuery(id+"F5.opExtrude","CAP_FACE",FACE,{"disambiguationData":[OSD([sQuery(id+"F4.wireOp",EDGE,"E9.bottom"),sQuery(id+"F4.wireOp",EDGE,"E9.top"),sQuery(id+"F4.wireOp",EDGE,"E9.left"),sQuery(id+"F4.wireOp",EDGE,"E9.right")])],"isStart":false});
            var sketch = newSketch(context, id + "F49", { "sketchPlane" : qUnion([Q0])});
            skLineSegment(sketch, "E110", {"start": v(-4690, 2050) * mm, "end": v(-4690, 950) * mm});
            skLineSegment(sketch, "E111", {"start": v(-4690, 2050) * mm, "end": v(-6240, 2050) * mm});
            skLineSegment(sketch, "E112", {"start": v(-6240, 2050) * mm, "end": v(-6240, 950) * mm});
            skLineSegment(sketch, "E113", {"start": v(-6240, 950) * mm, "end": v(-4690, 950) * mm});
            skSolve(sketch);
        }
        {
            var Q0;
            Q0 = qSketchRegion(id + "F49", true);
            var Q1;
            Q1=makeQuery(id+"F9.boolean.opBoolean","MERGE",FACE,{"derivedFrom":[makeQuery(id+"F7.boolean.opBoolean","COPY",FACE,{"derivedFrom":makeQuery(id+"F7.opExtrude","SWEPT_FACE",FACE,{"disambiguationData":[OSD([sQuery(id+"F6.wireOp",EDGE,"E10.left")])]})}),makeQuery(id+"F9.opExtrude","SWEPT_FACE",FACE,{"disambiguationData":[OSD([sQuery(id+"F8.wireOp",EDGE,"E11.left")])]})]});
            extrude(context, id + "F50", {"entities" : qUnion([Q0]), "operationType" : NewBodyOperationType.REMOVE, "endBound" : BoundingType.UP_TO_SURFACE, "oppositeDirection" : true, "endBoundEntityFace" : qUnion([Q1]), "depth" : 25 * mm});
        }
    });
